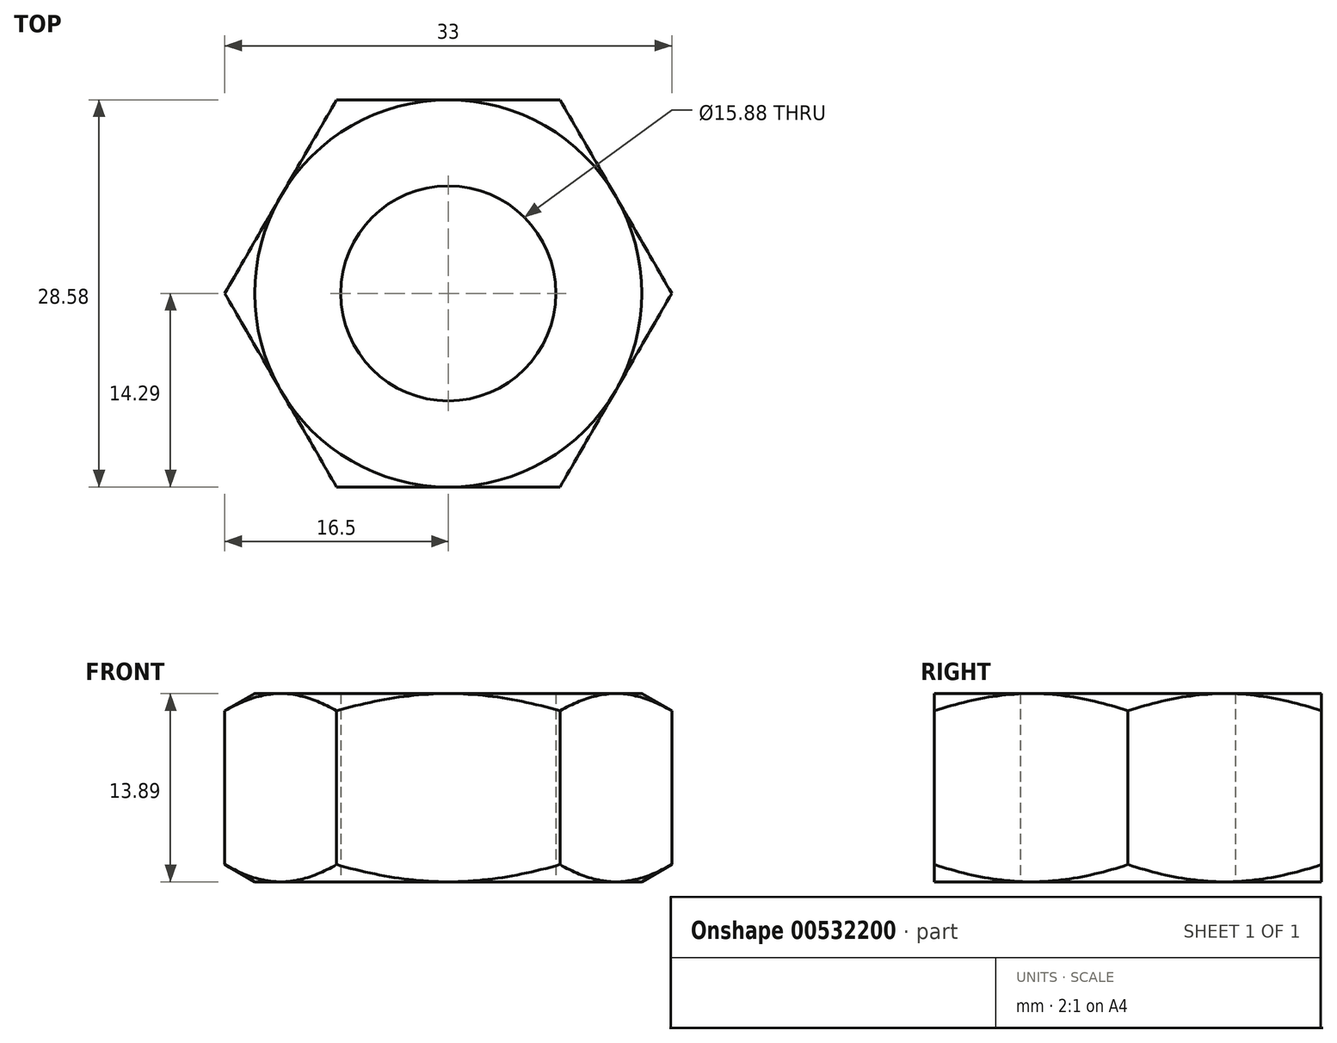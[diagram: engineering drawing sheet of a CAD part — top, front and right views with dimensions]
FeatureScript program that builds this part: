
annotation { "Feature Type Name" : "Feature", "Feature Type Description" : "" }
export const myFeature = defineFeature(function(context is Context, id is Id, definition is map)
    precondition{}
    {
        {
            var Q0;
            Q0=qCreatedBy(makeId("Top.planeOp"),FACE);
            var sketch = newSketch(context, id + "F0", { "sketchPlane" : qUnion([Q0])});
            skCircle(sketch, "E0", {"center": v(0, 0) * mm, "radius": 7.94 * mm});
            skCircle(sketch, "E1.cCircle", {"center": v(0, 0) * mm, "radius": 14.29 * mm, "construction": true});
            skLineSegment(sketch, "E1.0", {"start": v(8.25, 14.29) * mm, "end": v(16.5, 0) * mm});
            skLineSegment(sketch, "E1.1", {"start": v(16.5, 0) * mm, "end": v(8.25, -14.29) * mm});
            skLineSegment(sketch, "E1.2", {"start": v(8.25, -14.29) * mm, "end": v(-8.25, -14.29) * mm});
            skLineSegment(sketch, "E1.3", {"start": v(-8.25, -14.29) * mm, "end": v(-16.5, 0) * mm});
            skLineSegment(sketch, "E1.4", {"start": v(-16.5, 0) * mm, "end": v(-8.25, 14.29) * mm});
            skLineSegment(sketch, "E1.5", {"start": v(-8.25, 14.29) * mm, "end": v(8.25, 14.29) * mm});
            skPoint(sketch, "E1.0.midPoint", {"position": v(12.37, 7.14) * mm});
            skSolve(sketch);
        }
        {
            var Q0;
            Q0 = qSketchRegion(id + "F0", true);
            extrude(context, id + "F1", {"entities" : qUnion([Q0]), "depth" : 13.9 * mm, "offsetDistance" : 25.4 * mm});
        }
        {
            var Q0;
            Q0=qCreatedBy(makeId("Right.planeOp"),FACE);
            var sketch = newSketch(context, id + "F2", { "sketchPlane" : qUnion([Q0])});
            skLineSegment(sketch, "E2", {"start": v(0, 13.9) * mm, "end": v(0, 0) * mm, "construction": true});
            skLineSegment(sketch, "E3", {"start": v(14.29, 13.9) * mm, "end": v(23.81, 13.9) * mm});
            skLineSegment(sketch, "E4", {"start": v(23.81, 13.9) * mm, "end": v(23.81, 8.4) * mm});
            skLineSegment(sketch, "E5", {"start": v(23.81, 8.4) * mm, "end": v(14.29, 13.9) * mm});
            skLineSegment(sketch, "E6", {"start": v(14.29, 0) * mm, "end": v(23.81, 5.5) * mm});
            skLineSegment(sketch, "E7", {"start": v(23.81, 5.5) * mm, "end": v(23.81, 0) * mm});
            skLineSegment(sketch, "E8", {"start": v(23.81, 0) * mm, "end": v(14.29, 0) * mm});
            skSolve(sketch);
        }
        {
            var Q0;
            Q0 = qSketchRegion(id + "F2", true);
            var Q1;
            Q1=sQuery(id+"F2.wireOp",EDGE,"E2");
            revolve(context, id + "F3", {"operationType" : NewBodyOperationType.REMOVE, "entities" : qUnion([Q0]), "axis" : qUnion([Q1]), "revolveType" : RevolveType.FULL, "oppositeDirection" : true});
        }
    });
